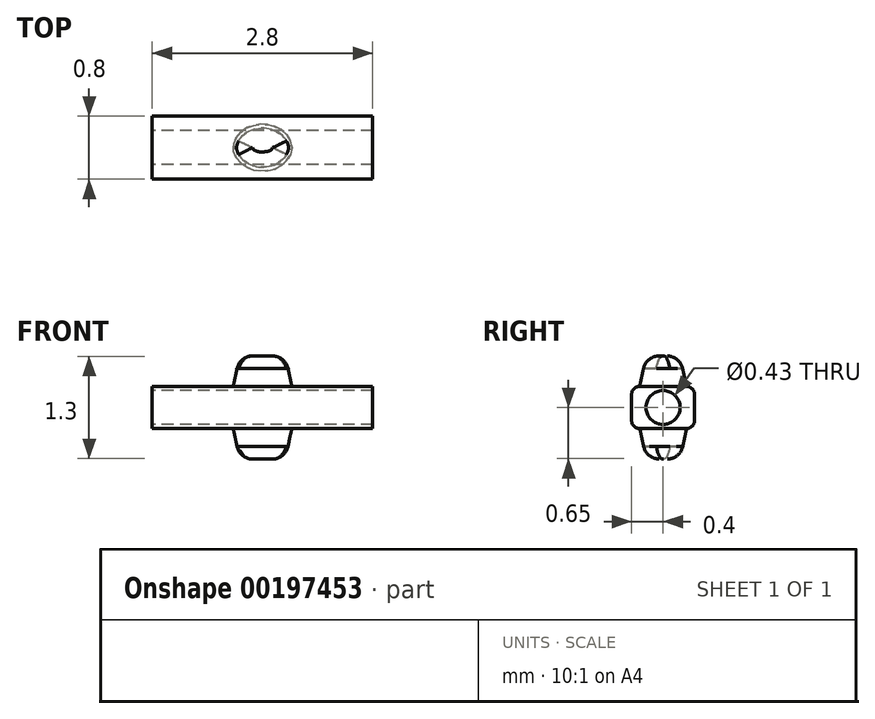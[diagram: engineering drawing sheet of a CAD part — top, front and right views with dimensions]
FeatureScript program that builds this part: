
annotation { "Feature Type Name" : "Feature", "Feature Type Description" : "" }
export const myFeature = defineFeature(function(context is Context, id is Id, definition is map)
    precondition{}
    {
        {
            var Q0;
            Q0=qCreatedBy(makeId("Top.planeOp"),FACE);
            var sketch = newSketch(context, id + "F0", { "sketchPlane" : qUnion([Q0])});
            skLineSegment(sketch, "E0.bottom", {"start": v(1.4, 0.4) * mm, "end": v(-1.4, 0.4) * mm});
            skLineSegment(sketch, "E0.top", {"start": v(1.4, -0.4) * mm, "end": v(-1.4, -0.4) * mm});
            skLineSegment(sketch, "E0.left", {"start": v(1.4, 0.4) * mm, "end": v(1.4, -0.4) * mm});
            skLineSegment(sketch, "E0.right", {"start": v(-1.4, 0.4) * mm, "end": v(-1.4, -0.4) * mm});
            skPoint(sketch, "E0.middle", {"position": v(0, 0) * mm});
            skSolve(sketch);
        }
        {
            var Q0;
            Q0 = qSketchRegion(id + "F0", true);
            extrude(context, id + "F1", {"entities" : qUnion([Q0]), "endBound" : BoundingType.SYMMETRIC, "depth" : 0.53 * mm, "offsetDistance" : 25 * mm});
        }
        {
            var Q0;
            Q0=qCreatedBy(makeId("Top.planeOp"),FACE);
            cPlane(context, id + "F2", {"entities" : qUnion([Q0]), "cplaneType" : CPlaneType.OFFSET, "offset" : 0.25 * mm, "width" : 152.4 * mm, "height" : 152.4 * mm});
        }
        {
            var Q0;
            Q0=qCreatedBy(id+"F2.planeOp",FACE);
            var sketch = newSketch(context, id + "F3", { "sketchPlane" : qUnion([Q0])});
            skPoint(sketch, "E1.middle", {"position": v(0, 0) * mm});
            skEllipse(sketch, "E2", {"center": v(0, 0) * mm, "majorRadius": 0.38 * mm, "minorRadius": 0.3 * mm, "majorAxis": v(1, 0)});
            skSolve(sketch);
        }
        {
            var Q0;
            Q0=qCreatedBy(makeId("Top.planeOp"),FACE);
            cPlane(context, id + "F4", {"entities" : qUnion([Q0]), "cplaneType" : CPlaneType.OFFSET, "offset" : 0.25 * mm, "oppositeDirection" : true, "width" : 152.4 * mm, "height" : 152.4 * mm});
        }
        {
            var Q0;
            Q0=qCreatedBy(id+"F4.planeOp",FACE);
            var sketch = newSketch(context, id + "F5", { "sketchPlane" : qUnion([Q0])});
            skPoint(sketch, "E3.middle", {"position": v(0, 0) * mm});
            skEllipse(sketch, "E4", {"center": v(0, 0) * mm, "majorRadius": 0.38 * mm, "minorRadius": 0.3 * mm, "majorAxis": v(1, 0)});
            skSolve(sketch);
        }
        {
            var Q0;
            Q0 = qSketchRegion(id + "F5", true);
            extrude(context, id + "F6", {"entities" : qUnion([Q0]), "operationType" : NewBodyOperationType.ADD, "oppositeDirection" : true, "depth" : .4 * mm, "hasDraft" : true, "draftAngle" : 12 * degree, "draftPullDirection" : true});
        }
        {
            var Q0;
            Q0 = qSketchRegion(id + "F3", true);
            extrude(context, id + "F7", {"entities" : qUnion([Q0]), "operationType" : NewBodyOperationType.ADD, "depth" : .4 * mm, "hasDraft" : true, "draftAngle" : 12 * degree, "draftPullDirection" : true});
        }
        {
            var Q0;
            Q0=makeQuery(id+"F1.opExtrude","CAP_EDGE",EDGE,{"disambiguationData":[OSD([sQuery(id+"F0.wireOp",EDGE,"E0.bottom")])],"isStart":false});
            var Q1;
            Q1=makeQuery(id+"F1.opExtrude","CAP_EDGE",EDGE,{"disambiguationData":[OSD([sQuery(id+"F0.wireOp",EDGE,"E0.bottom")])],"isStart":true});
            var Q2;
            Q2=makeQuery(id+"F1.opExtrude","CAP_EDGE",EDGE,{"disambiguationData":[OSD([sQuery(id+"F0.wireOp",EDGE,"E0.top")])],"isStart":false});
            var Q3;
            Q3=makeQuery(id+"F1.opExtrude","CAP_EDGE",EDGE,{"disambiguationData":[OSD([sQuery(id+"F0.wireOp",EDGE,"E0.top")])],"isStart":true});
            fillet(context, id + "F8", {"entities" : qUnion([Q0, Q1, Q2, Q3]), "radius" : .1 * mm, "allowEdgeOverflow" : false});
        }
        {
            var Q0;
            Q0=qCreatedBy(makeId("Right.planeOp"),FACE);
            var sketch = newSketch(context, id + "F9", { "sketchPlane" : qUnion([Q0])});
            skCircle(sketch, "E5", {"center": v(0, 0) * mm, "radius": 0.22 * mm});
            skSolve(sketch);
        }
        {
            var Q0;
            Q0 = qSketchRegion(id + "F9", true);
            extrude(context, id + "F10", {"entities" : qUnion([Q0]), "operationType" : NewBodyOperationType.REMOVE, "endBound" : BoundingType.SYMMETRIC, "depth" : 25.4 * mm});
        }
        {
            var Q0;
            Q0=makeQuery(id+"F7.opExtrude","CAP_EDGE",EDGE,{"disambiguationData":[OSD([sQuery(id+"F3.wireOp",EDGE,"E2")])],"isStart":false});
            fillet(context, id + "F11", {"entities" : qUnion([Q0]), "radius" : .2 * mm, "tangentPropagation" : true, "allowEdgeOverflow" : false});
        }
        {
            var Q0;
            Q0=makeQuery(id+"F6.opExtrude","CAP_EDGE",EDGE,{"disambiguationData":[OSD([sQuery(id+"F5.wireOp",EDGE,"E4")])],"isStart":false});
            fillet(context, id + "F12", {"entities" : qUnion([Q0]), "radius" : .2 * mm, "tangentPropagation" : true, "allowEdgeOverflow" : false});
        }
    });
